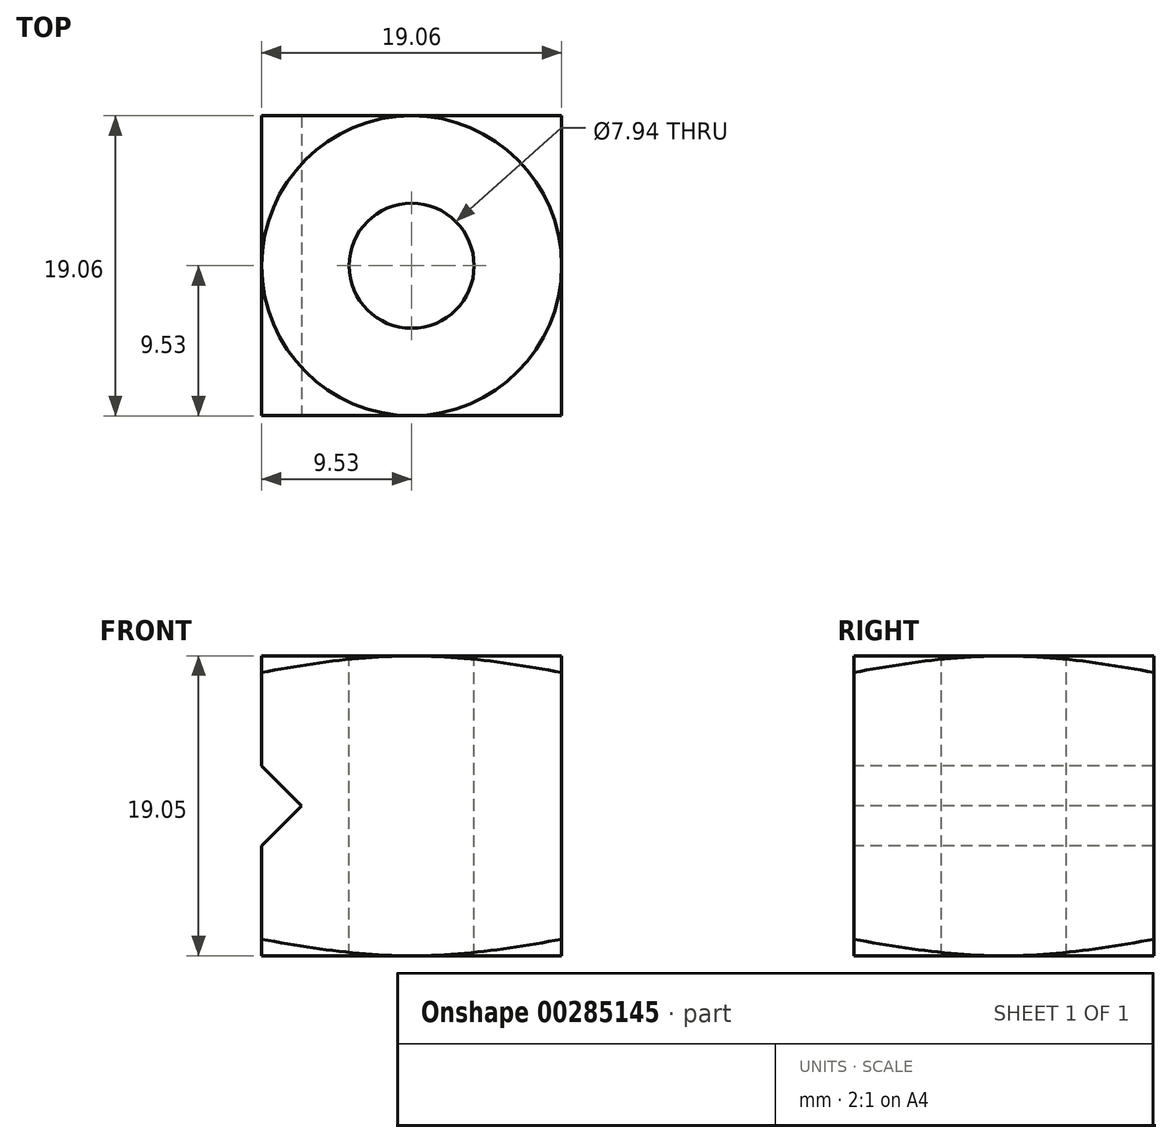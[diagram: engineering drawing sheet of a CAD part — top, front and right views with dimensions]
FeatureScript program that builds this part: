
annotation { "Feature Type Name" : "Feature", "Feature Type Description" : "" }
export const myFeature = defineFeature(function(context is Context, id is Id, definition is map)
    precondition{}
    {
        {
            var Q0;
            Q0=qCreatedBy(makeId("Top.planeOp"),FACE);
            var sketch = newSketch(context, id + "F0", { "sketchPlane" : qUnion([Q0])});
            skLineSegment(sketch, "E0.bottom", {"start": v(9.52, -9.53) * mm, "end": v(-9.52, -9.53) * mm});
            skLineSegment(sketch, "E0.top", {"start": v(9.53, 9.52) * mm, "end": v(-9.52, 9.52) * mm});
            skLineSegment(sketch, "E0.left", {"start": v(9.53, -9.53) * mm, "end": v(9.53, 9.52) * mm});
            skLineSegment(sketch, "E0.right", {"start": v(-9.53, -9.53) * mm, "end": v(-9.52, 9.52) * mm});
            skPoint(sketch, "E0.middle", {"position": v(0, 0) * mm});
            skSolve(sketch);
        }
        {
            var Q0;
            Q0 = qSketchRegion(id + "F0", true);
            extrude(context, id + "F1", {"entities" : qUnion([Q0]), "depth" : 19.05 * mm});
        }
        {
            var Q0;
            Q0=makeQuery(id+"F1.opExtrude","CAP_FACE",FACE,{"disambiguationData":[OSD([sQuery(id+"F0.wireOp",EDGE,"E0.bottom"),sQuery(id+"F0.wireOp",EDGE,"E0.top"),sQuery(id+"F0.wireOp",EDGE,"E0.left"),sQuery(id+"F0.wireOp",EDGE,"E0.right")])],"isStart":false});
            var sketch = newSketch(context, id + "F2", { "sketchPlane" : qUnion([Q0])});
            skCircle(sketch, "E1", {"center": v(0, 0) * mm, "radius": 9.53 * mm});
            skCircle(sketch, "E2", {"center": v(0, 0) * mm, "radius": 3.97 * mm});
            skSolve(sketch);
        }
        {
            var Q0;
            Q0=makeQuery(id+"F2.imprint","IMPRINT",FACE,{"disambiguationData":[TD([[makeQuery(id+"F2.imprint","IMPRINT",EDGE,{"derivedFrom":sQuery(id+"F2.wireOp",EDGE,"E2")}),1.0]])]});
            extrude(context, id + "F3", {"entities" : qUnion([Q0]), "operationType" : NewBodyOperationType.REMOVE, "oppositeDirection" : true, "depth" : 25.4 * mm});
        }
        {
            var Q0;
            Q0=makeQuery(id+"F1.opExtrude","CAP_FACE",FACE,{"disambiguationData":[OSD([sQuery(id+"F0.wireOp",EDGE,"E0.bottom"),sQuery(id+"F0.wireOp",EDGE,"E0.top"),sQuery(id+"F0.wireOp",EDGE,"E0.left"),sQuery(id+"F0.wireOp",EDGE,"E0.right")])],"isStart":true});
            var sketch = newSketch(context, id + "F4", { "sketchPlane" : qUnion([Q0])});
            skCircle(sketch, "E3", {"center": v(0, 0) * mm, "radius": 9.53 * mm});
            skSolve(sketch);
        }
        {
            var Q0;
            Q0=makeQuery(id+"F1.opExtrude","SWEPT_FACE",FACE,{"disambiguationData":[OSD([sQuery(id+"F0.wireOp",EDGE,"E0.left")])]});
            cPlane(context, id + "F5", {"entities" : qUnion([Q0]), "cplaneType" : CPlaneType.OFFSET, "offset" : 9.52 * mm, "oppositeDirection" : true, "width" : 152.4 * mm, "height" : 152.4 * mm});
        }
        {
            var Q0;
            Q0=qCreatedBy(id+"F5.planeOp",FACE);
            var sketch = newSketch(context, id + "F6", { "sketchPlane" : qUnion([Q0])});
            skPoint(sketch, "E4.0", {"position": v(9.52, 19.05) * mm});
            skPoint(sketch, "E5.0", {"position": v(9.52, 0) * mm});
            skLineSegment(sketch, "E6", {"start": v(9.52, 0) * mm, "end": v(23.93, 0) * mm});
            skLineSegment(sketch, "E7", {"start": v(23.93, 0) * mm, "end": v(23.93, 3.86) * mm});
            skLineSegment(sketch, "E8", {"start": v(23.93, 3.86) * mm, "end": v(9.52, 0) * mm});
            skSolve(sketch);
        }
        {
            var Q0;
            Q0=makeQuery(id+"F6.imprint","IMPRINT",FACE,{"disambiguationData":[TD([[makeQuery(id+"F6.imprint","IMPRINT",EDGE,{"derivedFrom":sQuery(id+"F6.wireOp",EDGE,"E6")}),1.0]])]});
            var Q1;
            Q1=sQuery(id+"F4.wireOp",EDGE,"E3");
            revolve(context, id + "F7", {"operationType" : NewBodyOperationType.REMOVE, "entities" : qUnion([Q0]), "axis" : qUnion([Q1]), "revolveType" : RevolveType.FULL, "oppositeDirection" : true});
        }
        {
            var Q0;
            Q0=qCreatedBy(id+"F5.planeOp",FACE);
            var sketch = newSketch(context, id + "F8", { "sketchPlane" : qUnion([Q0])});
            skLineSegment(sketch, "E9.0.0", {"start": v(-9.53, 19.05) * mm, "end": v(-9.53, 1.06) * mm});
            skFitSpline(sketch, "E9.0.1", {"points": [v(-9.53, 1.06) * mm, v(-7.95, 0.76) * mm, v(-5.57, 0.36) * mm, v(-2.39, 0.05) * mm, v(-0.8, 0) * mm, v(0, 0) * mm]});
            skFitSpline(sketch, "E9.0.2", {"points": [v(0, 0) * mm, v(0.8, 0) * mm, v(2.39, 0.05) * mm, v(4.78, 0.28) * mm, v(7.16, 0.63) * mm, v(8.74, 0.9) * mm, v(9.52, 1.06) * mm]});
            skLineSegment(sketch, "E9.0.3", {"start": v(9.52, 1.06) * mm, "end": v(9.52, 19.05) * mm});
            skLineSegment(sketch, "E9.0.4", {"start": v(9.52, 19.05) * mm, "end": v(-9.53, 19.05) * mm});
            skLineSegment(sketch, "E10", {"start": v(9.52, 19.05) * mm, "end": v(19.2, 19.05) * mm});
            skLineSegment(sketch, "E11", {"start": v(19.2, 19.05) * mm, "end": v(19.2, 16.46) * mm});
            skLineSegment(sketch, "E12", {"start": v(19.2, 16.46) * mm, "end": v(9.52, 19.05) * mm});
            skSolve(sketch);
        }
        {
            var Q0;
            Q0=makeQuery(id+"F8.imprint","IMPRINT",FACE,{"disambiguationData":[TD([[makeQuery(id+"F8.imprint","IMPRINT",EDGE,{"derivedFrom":sQuery(id+"F8.wireOp",EDGE,"E10")}),-1.0]])]});
            var Q1;
            Q1=sQuery(id+"F2.wireOp",EDGE,"E1");
            revolve(context, id + "F9", {"operationType" : NewBodyOperationType.REMOVE, "entities" : qUnion([Q0]), "axis" : qUnion([Q1]), "revolveType" : RevolveType.FULL, "oppositeDirection" : true});
        }
        {
            var Q0;
            Q0=makeQuery(id+"F1.opExtrude","SWEPT_FACE",FACE,{"disambiguationData":[OSD([sQuery(id+"F0.wireOp",EDGE,"E0.bottom")])]});
            var sketch = newSketch(context, id + "F10", { "sketchPlane" : qUnion([Q0])});
            skLineSegment(sketch, "E13", {"start": v(-9.53, 9.53) * mm, "end": v(-6.99, 9.53) * mm});
            skLineSegment(sketch, "E14", {"start": v(-6.99, 9.53) * mm, "end": v(-9.53, 12.07) * mm});
            skLineSegment(sketch, "E15", {"start": v(-6.99, 9.53) * mm, "end": v(-9.53, 6.99) * mm});
            skSolve(sketch);
        }
        {
            var Q0;
            {var subQ0=sQuery(id+"F10.wireOp",EDGE,"E13");Q0=makeQuery(id+"F10.imprint","IMPRINT",FACE,{"disambiguationData":[TD([[makeQuery(id+"F10.imprint","IMPRINT",EDGE,{"derivedFrom":subQ0}),1.0]])]});}
            var Q1;
            {var subQ0=sQuery(id+"F10.wireOp",EDGE,"E13");Q1=makeQuery(id+"F10.imprint","IMPRINT",FACE,{"disambiguationData":[TD([[makeQuery(id+"F10.imprint","IMPRINT",EDGE,{"derivedFrom":subQ0}),-1.0]])]});}
            extrude(context, id + "F11", {"entities" : qUnion([Q0, Q1]), "operationType" : NewBodyOperationType.REMOVE, "oppositeDirection" : true, "depth" : 25.4 * mm});
        }
    });
